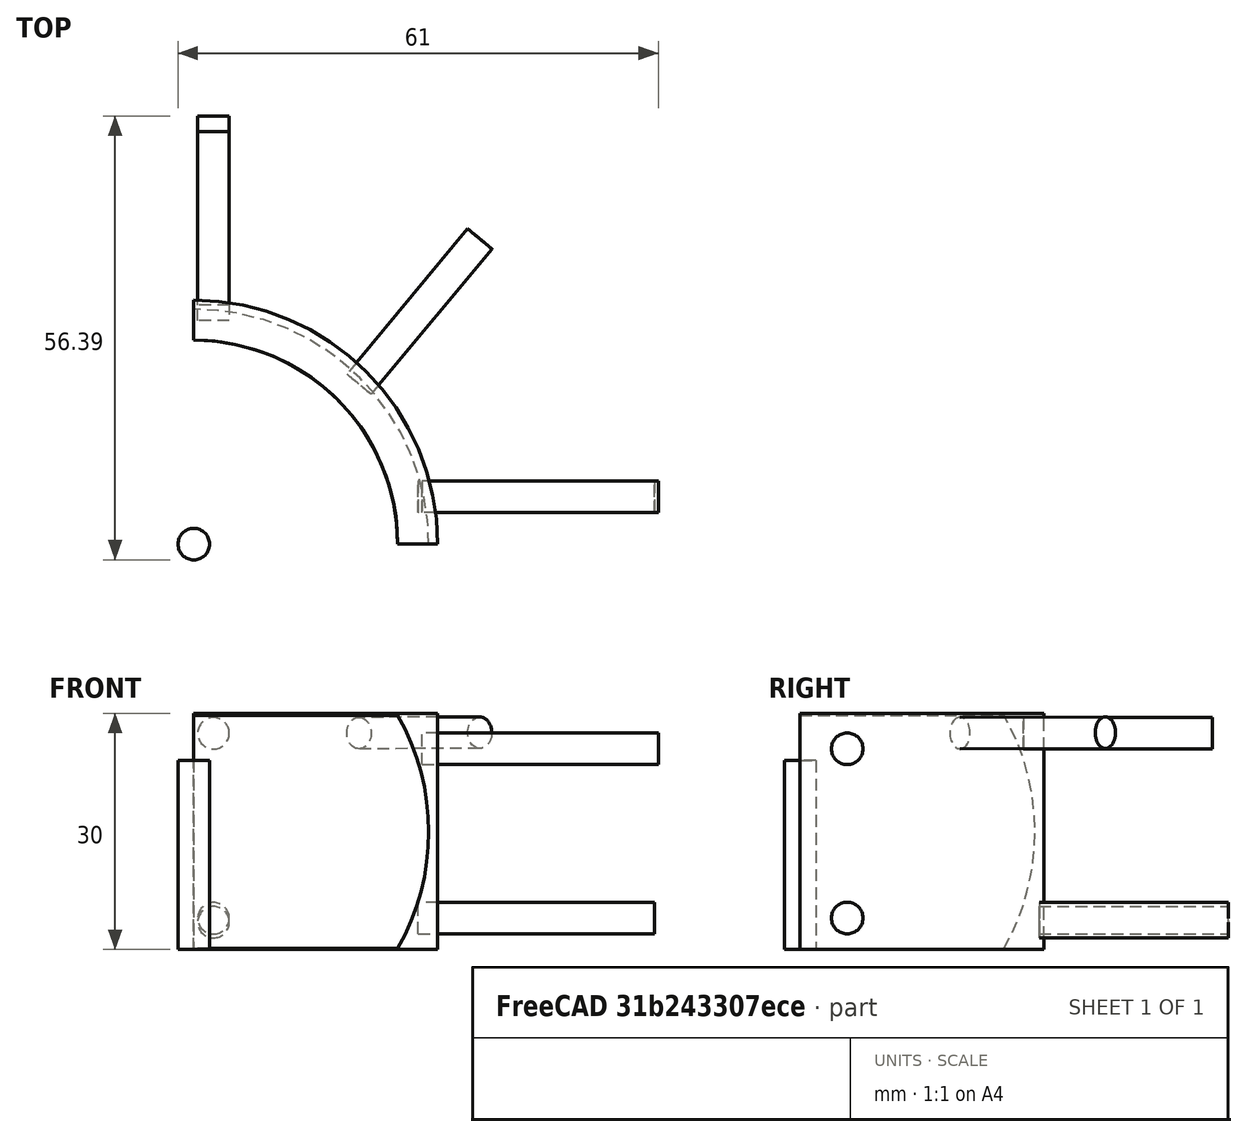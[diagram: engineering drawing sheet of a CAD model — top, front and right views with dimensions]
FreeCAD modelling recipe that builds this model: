
FCSTD DOCUMENT  (FreeCAD 1.1R43946 (Git))
Label: door_handle3
License: All rights reserved
LicenseURL: https://en.wikipedia.org/wiki/All_rights_reserved
objects: Part::Cylinder×7, Sketcher::SketchObject×3, App::Point×2, Mesh::Feature×1, PartDesign::FeatureBase×1, PartDesign::Pad×1, PartDesign::Groove×1, PartDesign::Body×1, App::Part×1
note: 22 computed .brp shape members not serialized (recipe doc carries the construction recipe); baked Part::Feature solids carry a one-line shape summary decoded from their .brp

FEATURE [Sketcher::SketchObject] Sketch
  ArcFitTolerance = 1e-06
  AttachmentSupport = -> [Origin]
  ExternalTypes = [0]
  FullyConstrained = true
  MakeInternals = false
  MapMode = 5
  sketch-geometry (6):
    g0: ArcOfCircle CenterX=0 CenterY=0 CenterZ=0 NormalX=0 NormalY=0 NormalZ=1 AngleXU=0 Radius=25.9 StartAngle=3.26795e-07 EndAngle=1.5708
    g1: LineSegment StartX=1.6e-15 StartY=25.9 StartZ=0 EndX=1.6e-15 EndY=30.9 EndZ=0
    g2: LineSegment StartX=25.9 StartY=8.46399e-06 StartZ=0 EndX=30.9 EndY=0 EndZ=0
    g3: ArcOfCircle CenterX=0 CenterY=0 CenterZ=0 NormalX=0 NormalY=0 NormalZ=1 AngleXU=0 Radius=30.98 StartAngle=0 EndAngle=1.5708
    g4: LineSegment StartX=30.9 StartY=0 StartZ=0 EndX=30.98 EndY=0 EndZ=0
    g5: LineSegment StartX=1.6e-15 StartY=30.9 StartZ=0 EndX=1.9e-15 EndY=30.98 EndZ=0
  constraints (18):
    c: Radius(g0) = 25.9
    c: Angle(g0) = 1.5708
    c: Coincident(g0,g-1)
    c: Distance(g1) = 5
    c: Coincident(g1,g0)
    c: PointOnObject(g1,g-2)
    c: Vertical(g1)
    c: Distance(g2) = 5
    c: Coincident(g2,g0)
    c: PointOnObject(g2,g-1)
    c: Radius(g3) = 30.98
    c: Coincident(g3,g0)
    c: PointOnObject(g3,g-2)
    c: PointOnObject(g3,g-1)
    c: Coincident(g4,g2)
    c: Coincident(g4,g3)
    c: Coincident(g5,g1)
    c: Coincident(g5,g3)
FEATURE [App::Point] Origin001
  Role = Origin
FEATURE [Sketcher::SketchObject] Sketch001
  ArcFitTolerance = 1e-06
  AttachmentSupport = -> [Origin]
  ExternalTypes = [0]
  FullyConstrained = false
  MakeInternals = false
  MapMode = 5
  Placement = pos=(0,0,0) rot=(1,0,0;1.5708rad)
  sketch-geometry (2):
    g0: ArcOfCircle CenterX=0 CenterY=14.9449 CenterZ=0 NormalX=0 NormalY=0 NormalZ=1 AngleXU=0 Radius=29.841 StartAngle=5.75864 EndAngle=6.80773
    g1: LineSegment StartX=25.8289 StartY=29.8898 StartZ=0 EndX=25.8289 EndY=-1.07e-14 EndZ=0
  constraints (5):
    c: PointOnObject(g0,g-2)
    c: PointOnObject(g0,g-1)
    c: Coincident(g1,g0)
    c: Coincident(g1,g0)
    c: Parallel(g1,g-2)
FEATURE [App::Point] Origin003
  Role = Origin
FEATURE [Mesh::Feature] doornob_arc
  Placement = pos=(191,148,0) rot=(0,0,1;3.14159rad)
FEATURE [Part::Cylinder] Cylinder006
  Angle = 360
  AttacherType = Attacher::AttachEngine3D
  FirstAngle = 0
  Height = 24
  Placement = pos=(2.5,52.39,27.47) rot=(1,0,0;1.5708rad)
  Radius = 2
  SecondAngle = 0
FEATURE [Part::Cylinder] Cylinder007
  Angle = 360
  AttacherType = Attacher::AttachEngine3D
  FirstAngle = 0
  Height = 24
  Placement = pos=(2.5,54.39,3.97) rot=(1,0,0;1.5708rad)
  Radius = 2
  SecondAngle = 0
FEATURE [Part::Cylinder] Cylinder
  Angle = 360
  AttacherType = Attacher::AttachEngine3D
  FirstAngle = 0
  Height = 30
  Placement = pos=(29,6,25.5) rot=(0,1,0;1.5708rad)
  Radius = 2
  SecondAngle = 0
FEATURE [Part::Cylinder] Cylinder008
  Angle = 360
  AttacherType = Attacher::AttachEngine3D
  FirstAngle = 0
  Height = 24
  Placement = pos=(2.5,54.39,3.47) rot=(1,0,0;1.5708rad)
  Radius = 2
  SecondAngle = 0
FEATURE [Part::Cylinder] Cylinder009
  Angle = 360
  AttacherType = Attacher::AttachEngine3D
  FirstAngle = 0
  Height = 24
  Placement = pos=(20.9857,20.3292,27.4999) rot=(0.39,-0.83,-0.39;4.5328rad)
  Radius = 2
  SecondAngle = 0
FEATURE [Part::Cylinder] Cylinder010
  Angle = 360
  AttacherType = Attacher::AttachEngine3D
  FirstAngle = 0
  Height = 30
  Placement = pos=(28.5,6,4) rot=(0,1,0;1.5708rad)
  Radius = 2
  SecondAngle = 0
FEATURE [Part::Cylinder] Cylinder011
  Angle = 360
  AttacherType = Attacher::AttachEngine3D
  FirstAngle = 0
  Height = 24
  Placement = pos=(21.03,20.35,4) rot=(0.39,-0.83,-0.39;4.5328rad)
  Radius = 2
  SecondAngle = 0
FEATURE [PartDesign::FeatureBase] BaseFeature
  BaseFeature = -> Cylinder011
  Suppressed = false
FEATURE [PartDesign::Pad] Pad
  BaseFeature = -> BaseFeature
  Direction = (0,0,1)
  Length = 30
  Length2 = 10
  Profile = -> Sketch
  ReferenceAxis = -> Sketch [N_Axis]
  Refine = true
  SideType = 0
  Suppressed = false
  Type = 0
  Type2 = 0
FEATURE [Sketcher::SketchObject] Sketch002
  ArcFitTolerance = 1e-06
  AttachmentSupport = -> [Pad]
  ExternalTypes = [0]
  FullyConstrained = true
  MakeInternals = false
  MapMode = 5
  Placement = pos=(1.9e-15,0,0) rot=(0.57735,-0.57735,-0.57735;2.0944rad)
FEATURE [PartDesign::Groove] Groove
  Angle = 360
  Angle2 = 0
  Axis = (0,2e-16,1)
  Base = (0,0,0)
  BaseFeature = -> Pad
  Profile = -> Sketch001
  ReferenceAxis = -> Sketch001 [V_Axis]
  Refine = true
  Suppressed = false
  Type = 0
FEATURE [PartDesign::Body] Body
  AllowCompound = true
  BaseFeature = -> Cylinder011
  Group = -> [BaseFeature,Sketch,Pad,Sketch001,Groove]
  Origin = -> Origin
  Tip = -> Groove
FEATURE [App::Part] Part
  Group = -> [Body,Cylinder010,Cylinder006,doornob_arc,Cylinder007,Cylinder,Cylinder011,Cylinder008,Cylinder009]
  Origin = -> Origin002
